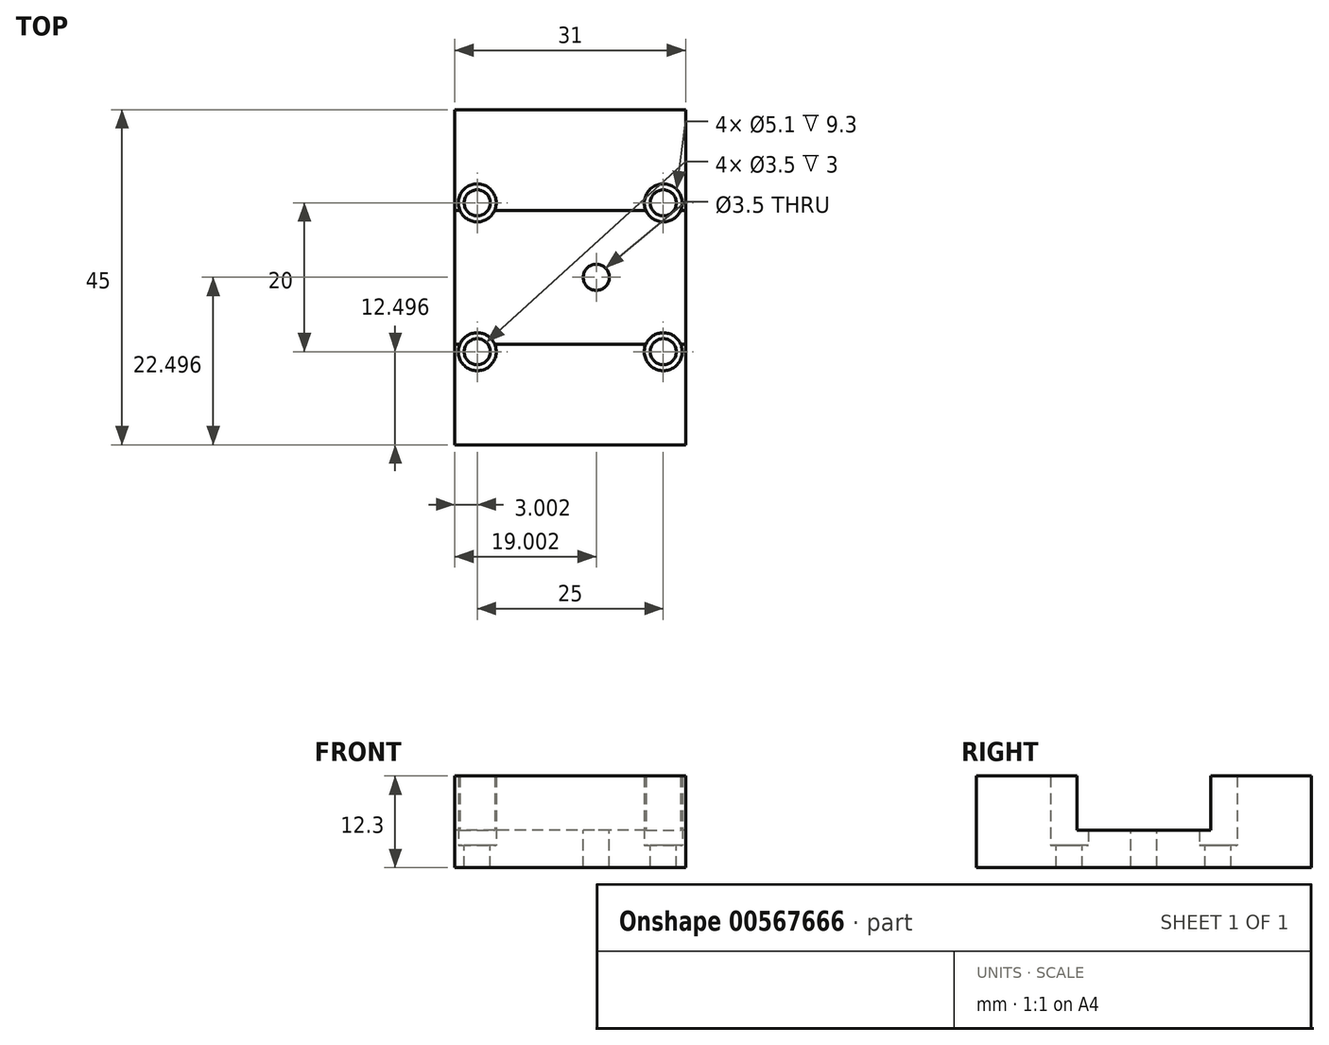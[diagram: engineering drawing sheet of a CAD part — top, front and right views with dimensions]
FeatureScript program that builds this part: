
annotation { "Feature Type Name" : "Feature", "Feature Type Description" : "" }
export const myFeature = defineFeature(function(context is Context, id is Id, definition is map)
    precondition{}
    {
        {
            var Q0;
            Q0=qCreatedBy(makeId("Top.planeOp"),FACE);
            var sketch = newSketch(context, id + "F0", { "sketchPlane" : qUnion([Q0])});
            skLineSegment(sketch, "E0.bottom", {"start": v(-8.49, 6.16) * mm, "end": v(22.51, 6.16) * mm});
            skLineSegment(sketch, "E0.top", {"start": v(-8.49, -38.84) * mm, "end": v(22.51, -38.84) * mm});
            skLineSegment(sketch, "E0.left", {"start": v(-8.49, 6.16) * mm, "end": v(-8.49, -38.84) * mm});
            skLineSegment(sketch, "E0.right", {"start": v(22.51, 6.16) * mm, "end": v(22.51, -38.84) * mm});
            skSolve(sketch);
        }
        {
            var Q0;
            Q0 = qSketchRegion(id + "F0", true);
            extrude(context, id + "F1", {"entities" : qUnion([Q0]), "depth" : 3 * mm, "offsetDistance" : 25 * mm});
        }
        {
            var Q0;
            Q0=makeQuery(id+"F1.opExtrude","CAP_FACE",FACE,{"disambiguationData":[OSD([sQuery(id+"F0.wireOp",EDGE,"E0.bottom"),sQuery(id+"F0.wireOp",EDGE,"E0.top"),sQuery(id+"F0.wireOp",EDGE,"E0.left"),sQuery(id+"F0.wireOp",EDGE,"E0.right")])],"isStart":false});
            var sketch = newSketch(context, id + "F2", { "sketchPlane" : qUnion([Q0])});
            skCircle(sketch, "E1", {"center": v(-5.49, -6.34) * mm, "radius": 1.75 * mm});
            skCircle(sketch, "E2", {"center": v(19.51, -6.34) * mm, "radius": 1.75 * mm});
            skCircle(sketch, "E3", {"center": v(19.51, -26.34) * mm, "radius": 1.75 * mm});
            skCircle(sketch, "E4", {"center": v(-5.49, -26.34) * mm, "radius": 1.75 * mm});
            skLineSegment(sketch, "E5.bottom", {"start": v(-8.49, -7.34) * mm, "end": v(22.51, -7.34) * mm});
            skLineSegment(sketch, "E5.top", {"start": v(-8.49, -25.34) * mm, "end": v(22.51, -25.34) * mm});
            skLineSegment(sketch, "E5.left", {"start": v(-8.49, -7.34) * mm, "end": v(-8.49, -25.34) * mm});
            skLineSegment(sketch, "E5.right", {"start": v(22.51, -7.34) * mm, "end": v(22.51, -25.34) * mm});
            skCircle(sketch, "E6", {"center": v(10.51, -16.34) * mm, "radius": 1.75 * mm});
            skPoint(sketch, "E6.centerSnap0", {"position": v(22.51, -16.34) * mm});
            skCircle(sketch, "E7.0", {"center": v(-5.49, -26.34) * mm, "radius": 2.55 * mm});
            skCircle(sketch, "E8.0", {"center": v(-5.49, -6.34) * mm, "radius": 2.55 * mm});
            skCircle(sketch, "E9.0", {"center": v(19.51, -6.34) * mm, "radius": 2.55 * mm});
            skCircle(sketch, "E10.0", {"center": v(19.51, -26.34) * mm, "radius": 2.55 * mm});
            skSolve(sketch);
        }
        {
            var Q0;
            Q0=makeQuery(id+"F2.imprint","IMPRINT",FACE,{"disambiguationData":[TD([[makeQuery(id+"F2.imprint","IMPRINT",EDGE,{"derivedFrom":sQuery(id+"F2.wireOp",EDGE,"E6")}),1.0]])]});
            extrude(context, id + "F3", {"entities" : qUnion([Q0]), "operationType" : NewBodyOperationType.REMOVE, "endBound" : BoundingType.UP_TO_NEXT, "oppositeDirection" : true, "depth" : 25 * mm, "offsetDistance" : 25 * mm});
        }
        {
            var Q0;
            {var subQ11=makeQuery(id+"F1.opExtrude","CAP_EDGE",EDGE,{"disambiguationData":[OSD([sQuery(id+"F0.wireOp",EDGE,"E0.top")])],"isStart":false});Q0=makeQuery(id+"F2.imprint","IMPRINT",FACE,{"disambiguationData":[TD([[makeQuery(id+"F2.imprint","IMPRINT",EDGE,{"derivedFrom":subQ11}),1.0]])]});}
            var Q1;
            {var subQ4=sQuery(id+"F2.wireOp",EDGE,"E5.left");Q1=makeQuery(id+"F2.imprint","IMPRINT",FACE,{"disambiguationData":[TD([[makeQuery(id+"F2.imprint","IMPRINT",EDGE,{"derivedFrom":subQ4}),1.0]])]});}
            var Q2;
            {var subQ11=makeQuery(id+"F1.opExtrude","CAP_EDGE",EDGE,{"disambiguationData":[OSD([sQuery(id+"F0.wireOp",EDGE,"E0.bottom")])],"isStart":false});Q2=makeQuery(id+"F2.imprint","IMPRINT",FACE,{"disambiguationData":[TD([[makeQuery(id+"F2.imprint","IMPRINT",EDGE,{"derivedFrom":subQ11}),-1.0]])]});}
            extrude(context, id + "F4", {"entities" : qUnion([Q0, Q1, Q2]), "operationType" : NewBodyOperationType.ADD, "depth" : 2 * mm, "offsetDistance" : 25 * mm});
        }
        {
            var Q0;
            {var subQ0=sQuery(id+"F2.wireOp",EDGE,"E5.top");var subQ1=sQuery(id+"F2.wireOp",EDGE,"E4");var subQ2=makeQuery(id+"F2.imprint","INTERSECT",VERTEX,{"disambiguationData":[OD(0.0)],"derivedFrom":[subQ1,subQ0]});Q0=makeQuery(id+"F2.imprint","IMPRINT",FACE,{"disambiguationData":[TD([[makeQuery(id+"F2.imprint","IMPRINT",EDGE,{"disambiguationData":[TD([[subQ2,-1.0]])],"derivedFrom":subQ1}),1.0]])]});}
            var Q1;
            {var subQ0=sQuery(id+"F2.wireOp",EDGE,"E5.top");var subQ1=sQuery(id+"F2.wireOp",EDGE,"E4");var subQ2=makeQuery(id+"F2.imprint","INTERSECT",VERTEX,{"disambiguationData":[OD(0.0)],"derivedFrom":[subQ1,subQ0]});Q1=makeQuery(id+"F2.imprint","IMPRINT",FACE,{"disambiguationData":[TD([[makeQuery(id+"F2.imprint","IMPRINT",EDGE,{"disambiguationData":[TD([[subQ2,1.0]])],"derivedFrom":subQ1}),1.0]])]});}
            var Q2;
            {var subQ0=sQuery(id+"F2.wireOp",EDGE,"E5.top");var subQ1=sQuery(id+"F2.wireOp",EDGE,"E3");var subQ2=makeQuery(id+"F2.imprint","INTERSECT",VERTEX,{"disambiguationData":[OD(0.0)],"derivedFrom":[subQ1,subQ0]});Q2=makeQuery(id+"F2.imprint","IMPRINT",FACE,{"disambiguationData":[TD([[makeQuery(id+"F2.imprint","IMPRINT",EDGE,{"disambiguationData":[TD([[subQ2,-1.0]])],"derivedFrom":subQ1}),1.0]])]});}
            var Q3;
            {var subQ0=sQuery(id+"F2.wireOp",EDGE,"E5.top");var subQ1=sQuery(id+"F2.wireOp",EDGE,"E3");var subQ2=makeQuery(id+"F2.imprint","INTERSECT",VERTEX,{"disambiguationData":[OD(0.0)],"derivedFrom":[subQ1,subQ0]});Q3=makeQuery(id+"F2.imprint","IMPRINT",FACE,{"disambiguationData":[TD([[makeQuery(id+"F2.imprint","IMPRINT",EDGE,{"disambiguationData":[TD([[subQ2,1.0]])],"derivedFrom":subQ1}),1.0]])]});}
            var Q4;
            {var subQ0=sQuery(id+"F2.wireOp",EDGE,"E5.bottom");var subQ1=sQuery(id+"F2.wireOp",EDGE,"E2");var subQ2=makeQuery(id+"F2.imprint","INTERSECT",VERTEX,{"disambiguationData":[OD(0.0)],"derivedFrom":[subQ1,subQ0]});Q4=makeQuery(id+"F2.imprint","IMPRINT",FACE,{"disambiguationData":[TD([[makeQuery(id+"F2.imprint","IMPRINT",EDGE,{"disambiguationData":[TD([[subQ2,-1.0]])],"derivedFrom":subQ1}),1.0]])]});}
            var Q5;
            {var subQ0=sQuery(id+"F2.wireOp",EDGE,"E5.bottom");var subQ1=sQuery(id+"F2.wireOp",EDGE,"E2");var subQ2=makeQuery(id+"F2.imprint","INTERSECT",VERTEX,{"disambiguationData":[OD(0.0)],"derivedFrom":[subQ1,subQ0]});Q5=makeQuery(id+"F2.imprint","IMPRINT",FACE,{"disambiguationData":[TD([[makeQuery(id+"F2.imprint","IMPRINT",EDGE,{"disambiguationData":[TD([[subQ2,1.0]])],"derivedFrom":subQ1}),1.0]])]});}
            var Q6;
            {var subQ0=sQuery(id+"F2.wireOp",EDGE,"E5.bottom");var subQ1=sQuery(id+"F2.wireOp",EDGE,"E1");var subQ2=makeQuery(id+"F2.imprint","INTERSECT",VERTEX,{"disambiguationData":[OD(0.0)],"derivedFrom":[subQ1,subQ0]});Q6=makeQuery(id+"F2.imprint","IMPRINT",FACE,{"disambiguationData":[TD([[makeQuery(id+"F2.imprint","IMPRINT",EDGE,{"disambiguationData":[TD([[subQ2,-1.0]])],"derivedFrom":subQ1}),1.0]])]});}
            var Q7;
            {var subQ0=sQuery(id+"F2.wireOp",EDGE,"E5.bottom");var subQ1=sQuery(id+"F2.wireOp",EDGE,"E1");var subQ2=makeQuery(id+"F2.imprint","INTERSECT",VERTEX,{"disambiguationData":[OD(0.0)],"derivedFrom":[subQ1,subQ0]});Q7=makeQuery(id+"F2.imprint","IMPRINT",FACE,{"disambiguationData":[TD([[makeQuery(id+"F2.imprint","IMPRINT",EDGE,{"disambiguationData":[TD([[subQ2,1.0]])],"derivedFrom":subQ1}),1.0]])]});}
            extrude(context, id + "F5", {"entities" : qUnion([Q0, Q1, Q2, Q3, Q4, Q5, Q6, Q7]), "operationType" : NewBodyOperationType.REMOVE, "endBound" : BoundingType.UP_TO_NEXT, "oppositeDirection" : true, "depth" : 25 * mm, "offsetDistance" : 25 * mm});
        }
        {
            var Q0;
            {var subQ11=makeQuery(id+"F1.opExtrude","CAP_EDGE",EDGE,{"disambiguationData":[OSD([sQuery(id+"F0.wireOp",EDGE,"E0.bottom")])],"isStart":false});Q0=makeQuery(id+"F2.imprint","IMPRINT",FACE,{"disambiguationData":[TD([[makeQuery(id+"F2.imprint","IMPRINT",EDGE,{"derivedFrom":subQ11}),-1.0]])]});}
            var Q1;
            {var subQ11=makeQuery(id+"F1.opExtrude","CAP_EDGE",EDGE,{"disambiguationData":[OSD([sQuery(id+"F0.wireOp",EDGE,"E0.top")])],"isStart":false});Q1=makeQuery(id+"F2.imprint","IMPRINT",FACE,{"disambiguationData":[TD([[makeQuery(id+"F2.imprint","IMPRINT",EDGE,{"derivedFrom":subQ11}),1.0]])]});}
            extrude(context, id + "F6", {"entities" : qUnion([Q0, Q1]), "operationType" : NewBodyOperationType.ADD, "depth" : (7.3 + 2) * mm, "offsetDistance" : 25 * mm});
        }
    });
